FREECAD ASSEMBLY — COMPONENT RECIPES ("cartridge-assembly")

This assembly document has 3 components, labeled P0..P2 below (a component is one placed body or linked part). 1 of them carries a construction recipe — the FreeCAD feature program that regenerates the part from scratch, quoted from this document or its linked companion documents; the rest are supplied as boundary geometry only. No exploded tour is included for this assembly.
COMPONENT P0 — geometry summary ("Body"; no construction recipe available for this part):
  bounding box: 57.9 x 23.5 x 13.0 mm
  tessellated surface: 1,632 triangles
  volume: 2424 mm^3 (14% of its bounding box)
  symmetry: mirror-symmetric across its x mid-plane, y mid-plane
COMPONENT P1 — recipe-attached ("Body002", a linked part whose construction recipe lives in a companion FreeCAD document of the same project; that document's serialized recipe follows).
Construction recipe (the companion document, serialized — sketch geometry with constraints, then the solid features built on it; lengths are millimeters unless a unit is written):

FCSTD DOCUMENT  (FreeCAD 1.1R20260106 (Git shallow))
Label: cartridge-gear
License: CERN Open Hardware Licence strongly-reciprocal
LicenseURL: https://cern-ohl.web.cern.ch/
objects: Sketcher::SketchObject×2, PartDesign::Pocket×2, Part::FeaturePython×1, PartDesign::FeatureBase×1, PartDesign::Fillet×1, PartDesign::Chamfer×1, PartDesign::Body×1, App::Point×1
note: 20 computed .brp shape members not serialized (recipe doc carries the construction recipe); baked Part::Feature solids carry a one-line shape summary decoded from their .brp

FEATURE [Part::FeaturePython] InvoluteGear  # WARN: FeaturePython — macro-defined, semantics opaque (R4)
  AttacherType = Attacher::AttachEngine3D
  angular_backlash = 0
  backlash = 0
  beta = 0
  clearance = 0.25
  da = 34
  df = 29.5
  double_helix = false
  dw = 32
  head = 0
  head_fillet = 0
  height = 4.5
  module = 1
  numpoints = 7
  pressure_angle = 20
  properties_from_tool = false
  reversed_backlash = false
  root_fillet = 0
  shift = 0
  simple = false
  teeth = 32
  transverse_pitch = 3.14159
  undercut = false
  version = 0.0.4
  expr: angular_backlash = backlash / dw * 360 ° / pi
  expr: dw = teeth * module
FEATURE [PartDesign::FeatureBase] BaseFeature
  BaseFeature = -> InvoluteGear
  Suppressed = false
FEATURE [Sketcher::SketchObject] Sketch
  ArcFitTolerance = 0
  AttachmentSupport = -> [XY_Plane001]
  ExternalTypes = [0]
  FullyConstrained = true
  MakeInternals = false
  MapMode = 5
  sketch-geometry (1):
    g0: Circle CenterX=0 CenterY=0 CenterZ=0 NormalX=0 NormalY=0 NormalZ=1 AngleXU=0 Radius=1.75
  constraints (2):
    c: Coincident(g0,g-1)
    c: Diameter(g0) = 3.5
FEATURE [PartDesign::Pocket] Pocket
  BaseFeature = -> BaseFeature
  Direction = (0,0,-1)
  Length = 5
  Length2 = 5
  Profile = -> Sketch
  ReferenceAxis = -> Sketch [N_Axis]
  Refine = true
  Reversed = true
  SideType = 0
  Suppressed = false
  Type = 0
  Type2 = 0
FEATURE [Sketcher::SketchObject] Sketch001
  ArcFitTolerance = 0
  AttachmentSupport = -> [XY_Plane001]
  ExternalTypes = [0]
  FullyConstrained = true
  MakeInternals = false
  MapMode = 5
  sketch-geometry (7):
    g0: LineSegment StartX=1.61658 StartY=2.8 StartZ=0 EndX=-1.61658 EndY=2.8 EndZ=0
    g1: LineSegment StartX=-1.61658 StartY=2.8 StartZ=0 EndX=-3.23316 EndY=5.0723e-12 EndZ=0
    g2: LineSegment StartX=-3.23316 StartY=5.0723e-12 StartZ=0 EndX=-1.61658 EndY=-2.8 EndZ=0
    g3: LineSegment StartX=-1.61658 StartY=-2.8 StartZ=0 EndX=1.61658 EndY=-2.8 EndZ=0
    g4: LineSegment StartX=1.61658 StartY=-2.8 StartZ=0 EndX=3.23316 EndY=5.8939e-12 EndZ=0
    g5: LineSegment StartX=3.23316 StartY=5.8939e-12 StartZ=0 EndX=1.61658 EndY=2.8 EndZ=0
    g6: Circle [constr] CenterX=0 CenterY=0 CenterZ=0 NormalX=0 NormalY=0 NormalZ=1 AngleXU=0 Radius=3.23316
  constraints (16):
    c: Coincident(g0,g1)
    c: Coincident(g1,g2)
    c: Coincident(g2,g3)
    c: Coincident(g3,g4)
    c: Coincident(g4,g5)
    c: Coincident(g5,g0)
    c: Equal(g0, g1-g5) x5
    c: PointOnObject(g0,g6)
    c: PointOnObject(g1,g6)
    c: PointOnObject(g2,g6)
    c: PointOnObject(g3,g6)
    c: PointOnObject(g4,g6)
    c: PointOnObject(g5,g6)
    c: Coincident(g6,g-1)
    c: Horizontal(g0)
    c: DistanceY(g2,g0) = 5.6
FEATURE [PartDesign::Pocket] Pocket001
  BaseFeature = -> Pocket
  Direction = (0,0,-1)
  Length = 3
  Length2 = 5
  Profile = -> Sketch001
  ReferenceAxis = -> Sketch001 [N_Axis]
  Refine = true
  Reversed = true
  SideType = 0
  Suppressed = false
  Type = 0
  Type2 = 0
FEATURE [PartDesign::Fillet] Fillet
  Base = -> Pocket001 [Edge204,Edge205,Edge200,Edge201,Edge202,Edge203]
  BaseFeature = -> Pocket001
  Radius = 0.4
  Refine = true
  SupportTransform = false
  Suppressed = false
  UseAllEdges = false
FEATURE [PartDesign::Chamfer] Chamfer
  Angle = 45
  Base = -> Fillet [Face206]
  BaseFeature = -> Fillet
  ChamferType = 0
  FlipDirection = false
  Refine = true
  Size = 0.2
  Size2 = 1
  SupportTransform = false
  Suppressed = false
  UseAllEdges = false
FEATURE [PartDesign::Body] Body001  label="Body"
  AllowCompound = false
  BaseFeature = -> InvoluteGear
  Group = -> [BaseFeature,Sketch,Pocket,Sketch001,Pocket001,Fillet,Chamfer]
  Origin = -> Origin001
  Tip = -> Chamfer
FEATURE [App::Point] Origin
  Role = Origin
COMPONENT P2 — geometry summary ("Body003"; no construction recipe available for this part):
  bounding box: 13.8 x 8.0 x 8.0 mm
  tessellated surface: 4,784 triangles
  volume: 523 mm^3 (59% of its bounding box)
  symmetry: revolution-symmetric about the z axis through its bounding-box center; mirror-symmetric across its x mid-plane, y mid-plane
PROVENANCE & LICENSES
A FreeCAD (.FCStd) document from a public repository crawl; recipes are the document's own serialized feature recipes (and, for linked parts, companion documents' recipes).
License: other.
